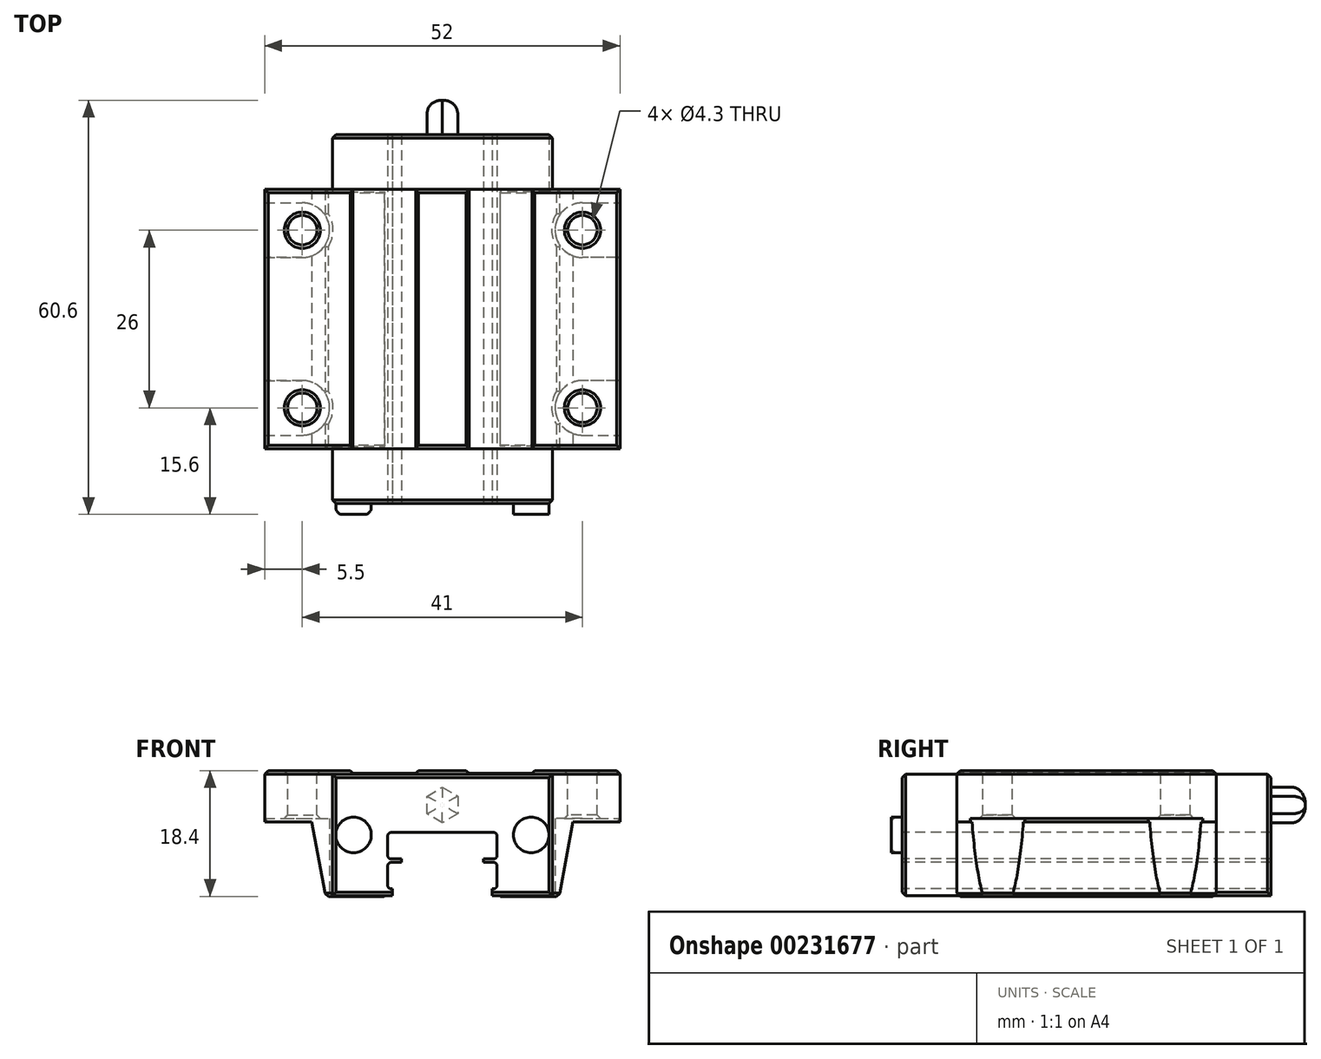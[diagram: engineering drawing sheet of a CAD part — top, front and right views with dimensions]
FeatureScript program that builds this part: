
annotation { "Feature Type Name" : "Feature", "Feature Type Description" : "" }
export const myFeature = defineFeature(function(context is Context, id is Id, definition is map)
    precondition{}
    {
        {
            var Q0;
            Q0=qCreatedBy(makeId("Front.planeOp"),FACE);
            var sketch = newSketch(context, id + "F0", { "sketchPlane" : qUnion([Q0])});
            skLineSegment(sketch, "E0", {"start": v(0, 7.25) * mm, "end": v(0, -7.25) * mm, "construction": true});
            skLineSegment(sketch, "E1", {"start": v(0, -7.25) * mm, "end": v(-7.5, -7.25) * mm});
            skLineSegment(sketch, "E2", {"start": v(-7.5, -7.25) * mm, "end": v(-7.5, -4.13) * mm});
            skLineSegment(sketch, "E3", {"start": v(-7.5, -4.13) * mm, "end": v(-7.5, -4.13) * mm});
            skLineSegment(sketch, "E4", {"start": v(-6.8, -3.43) * mm, "end": v(-6.8, -0.7) * mm});
            skLineSegment(sketch, "E5", {"start": v(-7.5, 0) * mm, "end": v(-7.5, 0) * mm});
            skLineSegment(sketch, "E6", {"start": v(-7.5, 0) * mm, "end": v(-7.5, 1.88) * mm});
            skLineSegment(sketch, "E7", {"start": v(-7.5, 1.88) * mm, "end": v(-7.5, 1.88) * mm});
            skLineSegment(sketch, "E8", {"start": v(-6.8, 2.88) * mm, "end": v(-5.5, 2.88) * mm});
            skLineSegment(sketch, "E9", {"start": v(-5.5, 2.88) * mm, "end": v(-5.5, 4.38) * mm});
            skLineSegment(sketch, "E10", {"start": v(-5.5, 4.38) * mm, "end": v(-6.8, 4.38) * mm});
            skLineSegment(sketch, "E11", {"start": v(-6.8, 4.38) * mm, "end": v(-6.8, 4.68) * mm});
            skLineSegment(sketch, "E12", {"start": v(-7.5, 5.38) * mm, "end": v(-7.5, 5.38) * mm});
            skLineSegment(sketch, "E13", {"start": v(-7.5, 5.38) * mm, "end": v(-7.5, 7.25) * mm});
            skLineSegment(sketch, "E14", {"start": v(-7.5, 7.25) * mm, "end": v(0, 7.25) * mm});
            skLineSegment(sketch, "E15", {"start": v(-6.8, 2.58) * mm, "end": v(-6.8, 2.87) * mm});
            skPoint(sketch, "E16.visualSharp", {"position": v(-6.8, -4.13) * mm});
            skArc(sketch, "E16.filletArc", {"start": v(-7.5, -4.13) * mm, "mid": v(-7, -3.92) * mm, "end": v(-6.8, -3.43) * mm});
            skPoint(sketch, "E17.visualSharp", {"position": v(-6.8, 0) * mm});
            skArc(sketch, "E17.filletArc", {"start": v(-6.8, -0.7) * mm, "mid": v(-7, -0.2) * mm, "end": v(-7.5, 0) * mm});
            skPoint(sketch, "E18.visualSharp", {"position": v(-6.8, 1.88) * mm});
            skArc(sketch, "E18.filletArc", {"start": v(-7.5, 1.88) * mm, "mid": v(-7, 2.08) * mm, "end": v(-6.8, 2.58) * mm});
            skPoint(sketch, "E19.visualSharp", {"position": v(-6.8, 5.38) * mm});
            skArc(sketch, "E19.filletArc", {"start": v(-6.8, 4.68) * mm, "mid": v(-7, 5.17) * mm, "end": v(-7.5, 5.38) * mm});
            skLineSegment(sketch, "E20.MirrorCS", {"start": v(6.8, 2.58) * mm, "end": v(6.8, 2.87) * mm});
            skLineSegment(sketch, "E21.MirrorCS", {"start": v(6.8, 4.38) * mm, "end": v(6.8, 4.68) * mm});
            skArc(sketch, "E22.MirrorCS", {"start": v(6.8, 4.68) * mm, "mid": v(7, 5.17) * mm, "end": v(7.5, 5.38) * mm});
            skArc(sketch, "E23.MirrorCS", {"start": v(7.5, 1.88) * mm, "mid": v(7, 2.08) * mm, "end": v(6.8, 2.58) * mm});
            skArc(sketch, "E24.MirrorCS", {"start": v(7.5, -4.13) * mm, "mid": v(7, -3.92) * mm, "end": v(6.8, -3.43) * mm});
            skArc(sketch, "E25.MirrorCS", {"start": v(6.8, -0.7) * mm, "mid": v(7, -0.2) * mm, "end": v(7.5, 0) * mm});
            skLineSegment(sketch, "E26.MirrorCS", {"start": v(7.5, 0) * mm, "end": v(7.5, 0) * mm});
            skLineSegment(sketch, "E27.MirrorCS", {"start": v(7.5, -7.25) * mm, "end": v(7.5, -4.13) * mm});
            skPoint(sketch, "E28.MirrorP", {"position": v(6.8, 0) * mm});
            skPoint(sketch, "E29.MirrorP", {"position": v(6.8, 5.38) * mm});
            skPoint(sketch, "E30.MirrorP", {"position": v(6.8, 1.88) * mm});
            skLineSegment(sketch, "E31.MirrorCS", {"start": v(7.5, -4.13) * mm, "end": v(7.5, -4.13) * mm});
            skLineSegment(sketch, "E32.MirrorCS", {"start": v(7.5, 1.88) * mm, "end": v(7.5, 1.88) * mm});
            skLineSegment(sketch, "E33.MirrorCS", {"start": v(7.5, 5.38) * mm, "end": v(7.5, 5.38) * mm});
            skLineSegment(sketch, "E34.MirrorCS", {"start": v(7.5, 5.38) * mm, "end": v(7.5, 7.25) * mm});
            skLineSegment(sketch, "E35.MirrorCS", {"start": v(5.5, 4.38) * mm, "end": v(6.8, 4.38) * mm});
            skLineSegment(sketch, "E36.MirrorCS", {"start": v(6.8, -3.43) * mm, "end": v(6.8, -0.7) * mm});
            skPoint(sketch, "E37.MirrorP", {"position": v(6.8, -4.13) * mm});
            skLineSegment(sketch, "E38.MirrorCS", {"start": v(6.8, 2.88) * mm, "end": v(5.5, 2.88) * mm});
            skLineSegment(sketch, "E39.MirrorCS", {"start": v(7.5, 0) * mm, "end": v(7.5, 1.88) * mm});
            skLineSegment(sketch, "E40.MirrorCS", {"start": v(5.5, 2.88) * mm, "end": v(5.5, 4.38) * mm});
            skLineSegment(sketch, "E41.MirrorCS", {"start": v(7.5, 7.25) * mm, "end": v(0, 7.25) * mm});
            skLineSegment(sketch, "E42.MirrorCS", {"start": v(0, -7.25) * mm, "end": v(7.5, -7.25) * mm});
            skSolve(sketch);
        }
        {
            var Q0;
            Q0=qCreatedBy(makeId("Front.planeOp"),FACE);
            var sketch = newSketch(context, id + "F1", { "sketchPlane" : qUnion([Q0])});
            skLineSegment(sketch, "E43", {"start": v(-16.1, 16.3) * mm, "end": v(-16.1, -1.5) * mm});
            skLineSegment(sketch, "E44", {"start": v(-16.1, -1.5) * mm, "end": v(-7.3, -1.5) * mm});
            skLineSegment(sketch, "E45", {"start": v(-7.3, -1.5) * mm, "end": v(-7.3, -0.5) * mm});
            skLineSegment(sketch, "E46", {"start": v(-7.3, -0.5) * mm, "end": v(-7.5, -0.5) * mm});
            skLineSegment(sketch, "E47", {"start": v(-8, 0) * mm, "end": v(-8, 2.88) * mm});
            skLineSegment(sketch, "E48", {"start": v(-7.5, 3.38) * mm, "end": v(-6, 3.38) * mm});
            skLineSegment(sketch, "E49", {"start": v(-6, 3.38) * mm, "end": v(-6, 3.88) * mm});
            skLineSegment(sketch, "E50", {"start": v(-6, 3.88) * mm, "end": v(-7.5, 3.88) * mm});
            skLineSegment(sketch, "E51", {"start": v(-8, 4.38) * mm, "end": v(-8, 7.25) * mm});
            skLineSegment(sketch, "E52", {"start": v(-7.5, 7.75) * mm, "end": v(0, 7.75) * mm});
            skLineSegment(sketch, "E53", {"start": v(-16.1, 16.3) * mm, "end": v(0, 16.3) * mm});
            skLineSegment(sketch, "E54", {"start": v(0, 16.3) * mm, "end": v(0, 0) * mm, "construction": true});
            skPoint(sketch, "E55.visualSharp", {"position": v(-8, 7.75) * mm});
            skArc(sketch, "E55.filletArc", {"start": v(-7.5, 7.75) * mm, "mid": v(-7.85, 7.6) * mm, "end": v(-8, 7.25) * mm});
            skPoint(sketch, "E56.visualSharp", {"position": v(-8, 3.88) * mm});
            skArc(sketch, "E56.filletArc", {"start": v(-8, 4.38) * mm, "mid": v(-7.85, 4.02) * mm, "end": v(-7.5, 3.88) * mm});
            skPoint(sketch, "E57.visualSharp", {"position": v(-8, 3.38) * mm});
            skArc(sketch, "E57.filletArc", {"start": v(-7.5, 3.38) * mm, "mid": v(-7.85, 3.23) * mm, "end": v(-8, 2.88) * mm});
            skPoint(sketch, "E58.visualSharp", {"position": v(-8, -0.5) * mm});
            skArc(sketch, "E58.filletArc", {"start": v(-8, 0) * mm, "mid": v(-7.85, -0.35) * mm, "end": v(-7.5, -0.5) * mm});
            skArc(sketch, "E59.MirrorCS", {"start": v(7.5, 7.75) * mm, "mid": v(7.85, 7.6) * mm, "end": v(8, 7.25) * mm});
            skArc(sketch, "E60.MirrorCS", {"start": v(7.5, 3.38) * mm, "mid": v(7.85, 3.23) * mm, "end": v(8, 2.88) * mm});
            skArc(sketch, "E61.MirrorCS", {"start": v(8, 0) * mm, "mid": v(7.85, -0.35) * mm, "end": v(7.5, -0.5) * mm});
            skLineSegment(sketch, "E62.MirrorCS", {"start": v(7.3, -0.5) * mm, "end": v(7.5, -0.5) * mm});
            skArc(sketch, "E63.MirrorCS", {"start": v(8, 4.38) * mm, "mid": v(7.85, 4.02) * mm, "end": v(7.5, 3.88) * mm});
            skLineSegment(sketch, "E64.MirrorCS", {"start": v(6, 3.88) * mm, "end": v(7.5, 3.88) * mm});
            skLineSegment(sketch, "E65.MirrorCS", {"start": v(8, 4.38) * mm, "end": v(8, 7.25) * mm});
            skLineSegment(sketch, "E66.MirrorCS", {"start": v(7.5, 3.38) * mm, "end": v(6, 3.38) * mm});
            skLineSegment(sketch, "E67.MirrorCS", {"start": v(7.3, -1.5) * mm, "end": v(7.3, -0.5) * mm});
            skLineSegment(sketch, "E68.MirrorCS", {"start": v(8, 0) * mm, "end": v(8, 2.88) * mm});
            skLineSegment(sketch, "E69.MirrorCS", {"start": v(6, 3.38) * mm, "end": v(6, 3.88) * mm});
            skPoint(sketch, "E70.MirrorP", {"position": v(8, 3.38) * mm});
            skPoint(sketch, "E71.MirrorP", {"position": v(8, 3.88) * mm});
            skLineSegment(sketch, "E72.MirrorCS", {"start": v(7.5, 7.75) * mm, "end": v(0, 7.75) * mm});
            skPoint(sketch, "E73.MirrorP", {"position": v(8, -0.5) * mm});
            skLineSegment(sketch, "E74.MirrorCS", {"start": v(16.1, 16.3) * mm, "end": v(0, 16.3) * mm});
            skLineSegment(sketch, "E75.MirrorCS", {"start": v(16.1, 16.3) * mm, "end": v(16.1, -1.5) * mm});
            skLineSegment(sketch, "E76.MirrorCS", {"start": v(16.1, -1.5) * mm, "end": v(7.3, -1.5) * mm});
            skPoint(sketch, "E77.MirrorP", {"position": v(8, 7.75) * mm});
            skSolve(sketch);
        }
        {
            var Q0;
            Q0 = qSketchRegion(id + "F1", true);
            extrude(context, id + "F2", {"entities" : qUnion([Q0]), "oppositeDirection" : true, "depth" : 54 * mm});
        }
        {
            var Q0;
            Q0=qCreatedBy(makeId("Front.planeOp"),FACE);
            cPlane(context, id + "F3", {"entities" : qUnion([Q0]), "cplaneType" : CPlaneType.OFFSET, "offset" : 8 * mm, "oppositeDirection" : true, "width" : 150 * mm, "height" : 150 * mm});
        }
        {
            var Q0;
            Q0=qCreatedBy(id+"F3.planeOp",FACE);
            var sketch = newSketch(context, id + "F4", { "sketchPlane" : qUnion([Q0])});
            skLineSegment(sketch, "E78", {"start": v(-8, -1.6) * mm, "end": v(-17.1, -1.6) * mm});
            skLineSegment(sketch, "E79", {"start": v(-17.1, -1.6) * mm, "end": v(-19.1, 9.3) * mm});
            skLineSegment(sketch, "E80", {"start": v(-19.1, 9.3) * mm, "end": v(-26, 9.3) * mm});
            skLineSegment(sketch, "E81", {"start": v(-26, 9.3) * mm, "end": v(-26, 16.8) * mm});
            skLineSegment(sketch, "E82", {"start": v(0, 16.8) * mm, "end": v(0, 0) * mm, "construction": true});
            skLineSegment(sketch, "E83", {"start": v(-26, 16.8) * mm, "end": v(-13, 16.8) * mm});
            skLineSegment(sketch, "E84", {"start": v(-13, 16.8) * mm, "end": v(-13, 16.4) * mm});
            skLineSegment(sketch, "E85", {"start": v(-13, 16.4) * mm, "end": v(-4, 16.4) * mm});
            skLineSegment(sketch, "E86", {"start": v(-4, 16.4) * mm, "end": v(-4, 16.8) * mm});
            skLineSegment(sketch, "E87", {"start": v(-4, 16.8) * mm, "end": v(0, 16.8) * mm});
            skLineSegment(sketch, "E88", {"start": v(-8, -1.6) * mm, "end": v(-8, 7.75) * mm});
            skLineSegment(sketch, "E89", {"start": v(-8, 7.75) * mm, "end": v(0, 7.75) * mm});
            skLineSegment(sketch, "E90.MirrorCS", {"start": v(4, 16.4) * mm, "end": v(4, 16.8) * mm});
            skLineSegment(sketch, "E91.MirrorCS", {"start": v(13, 16.8) * mm, "end": v(13, 16.4) * mm});
            skLineSegment(sketch, "E92.MirrorCS", {"start": v(8, -1.6) * mm, "end": v(8, 7.75) * mm});
            skLineSegment(sketch, "E93.MirrorCS", {"start": v(4, 16.8) * mm, "end": v(0, 16.8) * mm});
            skLineSegment(sketch, "E94.MirrorCS", {"start": v(26, 16.8) * mm, "end": v(13, 16.8) * mm});
            skLineSegment(sketch, "E95.MirrorCS", {"start": v(26, 9.3) * mm, "end": v(26, 16.8) * mm});
            skLineSegment(sketch, "E96.MirrorCS", {"start": v(8, -1.6) * mm, "end": v(17.1, -1.6) * mm});
            skLineSegment(sketch, "E97.MirrorCS", {"start": v(17.1, -1.6) * mm, "end": v(19.1, 9.3) * mm});
            skLineSegment(sketch, "E98.MirrorCS", {"start": v(8, 7.75) * mm, "end": v(0, 7.75) * mm});
            skLineSegment(sketch, "E99.MirrorCS", {"start": v(19.1, 9.3) * mm, "end": v(26, 9.3) * mm});
            skLineSegment(sketch, "E100.MirrorCS", {"start": v(13, 16.4) * mm, "end": v(4, 16.4) * mm});
            skSolve(sketch);
        }
        {
            var Q0;
            Q0 = qSketchRegion(id + "F4", true);
            extrude(context, id + "F5", {"entities" : qUnion([Q0]), "operationType" : NewBodyOperationType.ADD, "oppositeDirection" : true, "depth" : 38 * mm});
        }
        {
            var Q0;
            Q0=makeQuery(id+"F5.opExtrude","SWEPT_FACE",FACE,{"disambiguationData":[OSD([sQuery(id+"F4.wireOp",EDGE,"E83")])]});
            var sketch = newSketch(context, id + "F6", { "sketchPlane" : qUnion([Q0])});
            skCircle(sketch, "E101", {"center": v(-20.5, 40) * mm, "radius": 2.15 * mm});
            skCircle(sketch, "E102", {"center": v(-20.5, 14) * mm, "radius": 2.15 * mm});
            skLineSegment(sketch, "E103", {"start": v(-26, 27) * mm, "end": v(-13, 27) * mm, "construction": true});
            skCircle(sketch, "E104.MirrorC", {"center": v(20.5, 40) * mm, "radius": 2.15 * mm});
            skCircle(sketch, "E105.MirrorC", {"center": v(20.5, 14) * mm, "radius": 2.15 * mm});
            skSolve(sketch);
        }
        {
            var Q0;
            Q0 = qSketchRegion(id + "F6", true);
            extrude(context, id + "F7", {"entities" : qUnion([Q0]), "operationType" : NewBodyOperationType.REMOVE, "endBound" : BoundingType.THROUGH_ALL, "oppositeDirection" : true, "depth" : 25 * mm});
        }
        {
            var Q0;
            Q0=makeQuery(id+"F5.opExtrude","SWEPT_FACE",FACE,{"disambiguationData":[OSD([sQuery(id+"F4.wireOp",EDGE,"E80")])]});
            var sketch = newSketch(context, id + "F8", { "sketchPlane" : qUnion([Q0])});
            skArc(sketch, "E106", {"start": v(-20.5, -18) * mm, "mid": v(-16.5, -14) * mm, "end": v(-20.5, -10) * mm});
            skLineSegment(sketch, "E107", {"start": v(-26, -27) * mm, "end": v(-19.1, -27) * mm, "construction": true});
            skLineSegment(sketch, "E108", {"start": v(-20.5, -10) * mm, "end": v(-26, -10) * mm});
            skLineSegment(sketch, "E109", {"start": v(-26, -10) * mm, "end": v(-26, -18) * mm});
            skLineSegment(sketch, "E110", {"start": v(-26, -18) * mm, "end": v(-20.5, -18) * mm});
            skLineSegment(sketch, "E111.MirrorCS", {"start": v(-26, -36) * mm, "end": v(-20.5, -36) * mm});
            skLineSegment(sketch, "E112.MirrorCS", {"start": v(-26, -44) * mm, "end": v(-26, -36) * mm});
            skLineSegment(sketch, "E113.MirrorCS", {"start": v(-20.5, -44) * mm, "end": v(-26, -44) * mm});
            skArc(sketch, "E114.MirrorCS", {"start": v(-20.5, -36) * mm, "mid": v(-16.5, -40) * mm, "end": v(-20.5, -44) * mm});
            skArc(sketch, "E115.MirrorCS", {"start": v(20.5, -18) * mm, "mid": v(16.5, -14) * mm, "end": v(20.5, -10) * mm});
            skLineSegment(sketch, "E116.MirrorCS", {"start": v(26, -18) * mm, "end": v(20.5, -18) * mm});
            skLineSegment(sketch, "E117.MirrorCS", {"start": v(26, -10) * mm, "end": v(26, -18) * mm});
            skLineSegment(sketch, "E118.MirrorCS", {"start": v(20.5, -10) * mm, "end": v(26, -10) * mm});
            skLineSegment(sketch, "E119.MirrorCS", {"start": v(26, -36) * mm, "end": v(20.5, -36) * mm});
            skArc(sketch, "E120.MirrorCS", {"start": v(20.5, -36) * mm, "mid": v(16.5, -40) * mm, "end": v(20.5, -44) * mm});
            skLineSegment(sketch, "E121.MirrorCS", {"start": v(20.5, -44) * mm, "end": v(26, -44) * mm});
            skLineSegment(sketch, "E122.MirrorCS", {"start": v(26, -44) * mm, "end": v(26, -36) * mm});
            skSolve(sketch);
        }
        {
            var Q0;
            Q0 = qSketchRegion(id + "F8", true);
            extrude(context, id + "F9", {"entities" : qUnion([Q0]), "operationType" : NewBodyOperationType.REMOVE, "oppositeDirection" : true, "depth" : 0.5 * mm, "hasSecondDirection" : true, "secondDirectionBound" : SecondDirectionBoundingType.THROUGH_ALL, "secondDirectionOppositeDirection" : false, "secondDirectionDepth" : 25 * mm});
        }
        {
            var Q0;
            Q0=makeQuery(id+"F5.opExtrude","SWEPT_FACE",FACE,{"disambiguationData":[OSD([sQuery(id+"F4.wireOp",EDGE,"E78")])]});
            var Q1;
            Q1=makeQuery(id+"F5.opExtrude","SWEPT_FACE",FACE,{"disambiguationData":[OSD([sQuery(id+"F4.wireOp",EDGE,"E96.MirrorCS")])]});
            var Q2;
            Q2=makeQuery(id+"F7.boolean.opBoolean","COPY",FACE,{"derivedFrom":makeQuery(id+"F7.opExtrude","SWEPT_FACE",FACE,{"disambiguationData":[OSD([sQuery(id+"F6.wireOp",EDGE,"E101")])]})});
            var Q3;
            Q3=makeQuery(id+"F7.boolean.opBoolean","COPY",FACE,{"derivedFrom":makeQuery(id+"F7.opExtrude","SWEPT_FACE",FACE,{"disambiguationData":[OSD([sQuery(id+"F6.wireOp",EDGE,"E102")])]})});
            var Q4;
            Q4=makeQuery(id+"F7.boolean.opBoolean","COPY",FACE,{"derivedFrom":makeQuery(id+"F7.opExtrude","SWEPT_FACE",FACE,{"disambiguationData":[OSD([sQuery(id+"F6.wireOp",EDGE,"E105.MirrorC")])]})});
            var Q5;
            Q5=makeQuery(id+"F7.boolean.opBoolean","COPY",FACE,{"derivedFrom":makeQuery(id+"F7.opExtrude","SWEPT_FACE",FACE,{"disambiguationData":[OSD([sQuery(id+"F6.wireOp",EDGE,"E104.MirrorC")])]})});
            var Q6;
            Q6=makeQuery(id+"F5.opExtrude","SWEPT_FACE",FACE,{"disambiguationData":[OSD([sQuery(id+"F4.wireOp",EDGE,"E87"),sQuery(id+"F4.wireOp",EDGE,"E93.MirrorCS")])]});
            var Q7;
            Q7=makeQuery(id+"F5.opExtrude","SWEPT_FACE",FACE,{"disambiguationData":[OSD([sQuery(id+"F4.wireOp",EDGE,"E94.MirrorCS")])]});
            var Q8;
            Q8=makeQuery(id+"F5.opExtrude","SWEPT_FACE",FACE,{"disambiguationData":[OSD([sQuery(id+"F4.wireOp",EDGE,"E83")])]});
            chamfer(context, id + "F10", {"entities" : qUnion([Q0, Q1, Q2, Q3, Q4, Q5, Q6, Q7, Q8]), "width" : 0.5 * mm, "tangentPropagation" : true});
        }
        {
            var Q0;
            {var subQ0=sQuery(id+"F4.wireOp",EDGE,"E95.MirrorCS");var subQ1=sQuery(id+"F4.wireOp",EDGE,"E99.MirrorCS");Q0=makeQuery(id+"F9.boolean.opBoolean","SPLIT",EDGE,{"disambiguationData":[TD([makeQuery(id+"F9.opExtrude","SWEPT_FACE",FACE,{"disambiguationData":[OSD([sQuery(id+"F8.wireOp",EDGE,"E116.MirrorCS")])]})])],"derivedFrom":makeQuery(id+"F5.opExtrude","SWEPT_EDGE",EDGE,{"disambiguationData":[OSD([subQ0,subQ1])]})});}
            var Q1;
            {var subQ0=sQuery(id+"F1.wireOp",EDGE,"E76.MirrorCS");var subQ1=sQuery(id+"F1.wireOp",EDGE,"E75.MirrorCS");Q1=makeQuery(id+"F5.boolean.opBoolean","SPLIT",EDGE,{"disambiguationData":[TD([makeQuery(id+"F5.opExtrude","CAP_FACE",FACE,{"disambiguationData":[OSD([sQuery(id+"F4.wireOp",EDGE,"E78"),sQuery(id+"F4.wireOp",EDGE,"E79"),sQuery(id+"F4.wireOp",EDGE,"E80"),sQuery(id+"F4.wireOp",EDGE,"E81"),sQuery(id+"F4.wireOp",EDGE,"E83"),sQuery(id+"F4.wireOp",EDGE,"E84"),sQuery(id+"F4.wireOp",EDGE,"E85"),sQuery(id+"F4.wireOp",EDGE,"E86"),sQuery(id+"F4.wireOp",EDGE,"E87"),sQuery(id+"F4.wireOp",EDGE,"E88"),sQuery(id+"F4.wireOp",EDGE,"E89"),sQuery(id+"F4.wireOp",EDGE,"E90.MirrorCS"),sQuery(id+"F4.wireOp",EDGE,"E91.MirrorCS"),sQuery(id+"F4.wireOp",EDGE,"E92.MirrorCS"),sQuery(id+"F4.wireOp",EDGE,"E93.MirrorCS"),sQuery(id+"F4.wireOp",EDGE,"E94.MirrorCS"),sQuery(id+"F4.wireOp",EDGE,"E95.MirrorCS"),sQuery(id+"F4.wireOp",EDGE,"E96.MirrorCS"),sQuery(id+"F4.wireOp",EDGE,"E97.MirrorCS"),sQuery(id+"F4.wireOp",EDGE,"E98.MirrorCS"),sQuery(id+"F4.wireOp",EDGE,"E99.MirrorCS"),sQuery(id+"F4.wireOp",EDGE,"E100.MirrorCS")])],"isStart":false})])],"derivedFrom":makeQuery(id+"F2.opExtrude","SWEPT_EDGE",EDGE,{"disambiguationData":[OSD([subQ1,subQ0])]})});}
            var Q2;
            Q2=makeQuery(id+"F2.opExtrude","CAP_EDGE",EDGE,{"disambiguationData":[OSD([sQuery(id+"F1.wireOp",EDGE,"E75.MirrorCS")])],"isStart":false});
            var Q3;
            Q3=makeQuery(id+"F2.opExtrude","CAP_EDGE",EDGE,{"disambiguationData":[OSD([sQuery(id+"F1.wireOp",EDGE,"E53"),sQuery(id+"F1.wireOp",EDGE,"E74.MirrorCS")])],"isStart":false});
            var Q4;
            Q4=makeQuery(id+"F2.opExtrude","CAP_EDGE",EDGE,{"disambiguationData":[OSD([sQuery(id+"F1.wireOp",EDGE,"E43")])],"isStart":false});
            var Q5;
            Q5=makeQuery(id+"F2.opExtrude","CAP_EDGE",EDGE,{"disambiguationData":[OSD([sQuery(id+"F1.wireOp",EDGE,"E44")])],"isStart":false});
            var Q6;
            Q6=makeQuery(id+"F2.opExtrude","CAP_EDGE",EDGE,{"disambiguationData":[OSD([sQuery(id+"F1.wireOp",EDGE,"E43")])],"isStart":true});
            var Q7;
            Q7=makeQuery(id+"F2.opExtrude","CAP_EDGE",EDGE,{"disambiguationData":[OSD([sQuery(id+"F1.wireOp",EDGE,"E44")])],"isStart":true});
            var Q8;
            Q8=makeQuery(id+"F2.opExtrude","CAP_EDGE",EDGE,{"disambiguationData":[OSD([sQuery(id+"F1.wireOp",EDGE,"E76.MirrorCS")])],"isStart":true});
            var Q9;
            Q9=makeQuery(id+"F2.opExtrude","CAP_EDGE",EDGE,{"disambiguationData":[OSD([sQuery(id+"F1.wireOp",EDGE,"E75.MirrorCS")])],"isStart":true});
            var Q10;
            Q10=makeQuery(id+"F2.opExtrude","CAP_EDGE",EDGE,{"disambiguationData":[OSD([sQuery(id+"F1.wireOp",EDGE,"E53"),sQuery(id+"F1.wireOp",EDGE,"E74.MirrorCS")])],"isStart":true});
            var Q11;
            {var subQ0=sQuery(id+"F4.wireOp",EDGE,"E80");var subQ1=sQuery(id+"F4.wireOp",EDGE,"E81");Q11=makeQuery(id+"F9.boolean.opBoolean","SPLIT",EDGE,{"disambiguationData":[TD([makeQuery(id+"F9.opExtrude","SWEPT_FACE",FACE,{"disambiguationData":[OSD([sQuery(id+"F8.wireOp",EDGE,"E110")])]})])],"derivedFrom":makeQuery(id+"F5.opExtrude","SWEPT_EDGE",EDGE,{"disambiguationData":[OSD([subQ0,subQ1])]})});}
            chamfer(context, id + "F11", {"entities" : qUnion([Q0, Q1, Q2, Q3, Q4, Q5, Q6, Q7, Q8, Q9, Q10, Q11]), "width" : 0.5 * mm, "tangentPropagation" : true});
        }
        {
            var Q0;
            Q0=makeQuery(id+"F2.opExtrude","CAP_FACE",FACE,{"disambiguationData":[OSD([sQuery(id+"F1.wireOp",EDGE,"E43"),sQuery(id+"F1.wireOp",EDGE,"E44"),sQuery(id+"F1.wireOp",EDGE,"E45"),sQuery(id+"F1.wireOp",EDGE,"E46"),sQuery(id+"F1.wireOp",EDGE,"E47"),sQuery(id+"F1.wireOp",EDGE,"E48"),sQuery(id+"F1.wireOp",EDGE,"E49"),sQuery(id+"F1.wireOp",EDGE,"E50"),sQuery(id+"F1.wireOp",EDGE,"E51"),sQuery(id+"F1.wireOp",EDGE,"E52"),sQuery(id+"F1.wireOp",EDGE,"E53"),sQuery(id+"F1.wireOp",EDGE,"E55.filletArc"),sQuery(id+"F1.wireOp",EDGE,"E56.filletArc"),sQuery(id+"F1.wireOp",EDGE,"E57.filletArc"),sQuery(id+"F1.wireOp",EDGE,"E58.filletArc"),sQuery(id+"F1.wireOp",EDGE,"E59.MirrorCS"),sQuery(id+"F1.wireOp",EDGE,"E60.MirrorCS"),sQuery(id+"F1.wireOp",EDGE,"E61.MirrorCS"),sQuery(id+"F1.wireOp",EDGE,"E62.MirrorCS"),sQuery(id+"F1.wireOp",EDGE,"E63.MirrorCS"),sQuery(id+"F1.wireOp",EDGE,"E64.MirrorCS"),sQuery(id+"F1.wireOp",EDGE,"E65.MirrorCS"),sQuery(id+"F1.wireOp",EDGE,"E66.MirrorCS"),sQuery(id+"F1.wireOp",EDGE,"E67.MirrorCS"),sQuery(id+"F1.wireOp",EDGE,"E68.MirrorCS"),sQuery(id+"F1.wireOp",EDGE,"E69.MirrorCS"),sQuery(id+"F1.wireOp",EDGE,"E72.MirrorCS"),sQuery(id+"F1.wireOp",EDGE,"E74.MirrorCS"),sQuery(id+"F1.wireOp",EDGE,"E75.MirrorCS"),sQuery(id+"F1.wireOp",EDGE,"E76.MirrorCS")])],"isStart":true});
            var sketch = newSketch(context, id + "F12", { "sketchPlane" : qUnion([Q0])});
            skLineSegment(sketch, "E123", {"start": v(-15.6, 7.4) * mm, "end": v(15.6, 7.4) * mm, "construction": true});
            skCircle(sketch, "E124", {"center": v(-13, 7.4) * mm, "radius": 2.6 * mm});
            skLineSegment(sketch, "E125", {"start": v(0, 0) * mm, "end": v(0, 15.8) * mm, "construction": true});
            skCircle(sketch, "E126", {"center": v(13, 7.4) * mm, "radius": 2.6 * mm});
            skSolve(sketch);
        }
        {
            var Q0;
            Q0 = qSketchRegion(id + "F12", true);
            extrude(context, id + "F13", {"entities" : qUnion([Q0]), "operationType" : NewBodyOperationType.ADD, "depth" : 1.6 * mm});
        }
        {
            var Q0;
            Q0=makeQuery(id+"F2.opExtrude","CAP_FACE",FACE,{"disambiguationData":[OSD([sQuery(id+"F1.wireOp",EDGE,"E43"),sQuery(id+"F1.wireOp",EDGE,"E44"),sQuery(id+"F1.wireOp",EDGE,"E45"),sQuery(id+"F1.wireOp",EDGE,"E46"),sQuery(id+"F1.wireOp",EDGE,"E47"),sQuery(id+"F1.wireOp",EDGE,"E48"),sQuery(id+"F1.wireOp",EDGE,"E49"),sQuery(id+"F1.wireOp",EDGE,"E50"),sQuery(id+"F1.wireOp",EDGE,"E51"),sQuery(id+"F1.wireOp",EDGE,"E52"),sQuery(id+"F1.wireOp",EDGE,"E53"),sQuery(id+"F1.wireOp",EDGE,"E55.filletArc"),sQuery(id+"F1.wireOp",EDGE,"E56.filletArc"),sQuery(id+"F1.wireOp",EDGE,"E57.filletArc"),sQuery(id+"F1.wireOp",EDGE,"E58.filletArc"),sQuery(id+"F1.wireOp",EDGE,"E59.MirrorCS"),sQuery(id+"F1.wireOp",EDGE,"E60.MirrorCS"),sQuery(id+"F1.wireOp",EDGE,"E61.MirrorCS"),sQuery(id+"F1.wireOp",EDGE,"E62.MirrorCS"),sQuery(id+"F1.wireOp",EDGE,"E63.MirrorCS"),sQuery(id+"F1.wireOp",EDGE,"E64.MirrorCS"),sQuery(id+"F1.wireOp",EDGE,"E65.MirrorCS"),sQuery(id+"F1.wireOp",EDGE,"E66.MirrorCS"),sQuery(id+"F1.wireOp",EDGE,"E67.MirrorCS"),sQuery(id+"F1.wireOp",EDGE,"E68.MirrorCS"),sQuery(id+"F1.wireOp",EDGE,"E69.MirrorCS"),sQuery(id+"F1.wireOp",EDGE,"E72.MirrorCS"),sQuery(id+"F1.wireOp",EDGE,"E74.MirrorCS"),sQuery(id+"F1.wireOp",EDGE,"E75.MirrorCS"),sQuery(id+"F1.wireOp",EDGE,"E76.MirrorCS")])],"isStart":false});
            var sketch = newSketch(context, id + "F14", { "sketchPlane" : qUnion([Q0])});
            skLineSegment(sketch, "E127", {"start": v(0, 15.8) * mm, "end": v(0, 7.75) * mm, "construction": true});
            skCircle(sketch, "E128", {"center": v(0, 11.78) * mm, "radius": 2.6 * mm, "construction": true});
            skLineSegment(sketch, "E129", {"start": v(-2.25, 13.07) * mm, "end": v(-2.25, 10.48) * mm});
            skLineSegment(sketch, "E130", {"start": v(-2.25, 10.48) * mm, "end": v(0, 9.18) * mm});
            skLineSegment(sketch, "E131", {"start": v(0, 9.18) * mm, "end": v(2.25, 10.48) * mm});
            skLineSegment(sketch, "E132", {"start": v(2.25, 10.48) * mm, "end": v(2.25, 13.07) * mm});
            skLineSegment(sketch, "E133", {"start": v(2.25, 13.07) * mm, "end": v(0, 14.37) * mm});
            skLineSegment(sketch, "E134", {"start": v(0, 14.37) * mm, "end": v(-2.25, 13.07) * mm});
            skSolve(sketch);
        }
        {
            var Q0;
            Q0 = qSketchRegion(id + "F14", true);
            extrude(context, id + "F15", {"entities" : qUnion([Q0]), "operationType" : NewBodyOperationType.ADD, "depth" : 5 * mm});
        }
        {
            var Q0;
            Q0=makeQuery(id+"F15.opExtrude","CAP_FACE",FACE,{"disambiguationData":[OSD([sQuery(id+"F14.wireOp",EDGE,"E129"),sQuery(id+"F14.wireOp",EDGE,"E130"),sQuery(id+"F14.wireOp",EDGE,"E131"),sQuery(id+"F14.wireOp",EDGE,"E132"),sQuery(id+"F14.wireOp",EDGE,"E133"),sQuery(id+"F14.wireOp",EDGE,"E134")])],"isStart":false});
            fillet(context, id + "F16", {"entities" : qUnion([Q0]), "radius" : 2 * mm, "tangentPropagation" : true, "allowEdgeOverflow" : false});
        }
        {
            var Q0;
            Q0=makeQuery(id+"F13.opExtrude","CAP_EDGE",EDGE,{"disambiguationData":[OSD([sQuery(id+"F12.wireOp",EDGE,"E124")])],"isStart":false});
            fillet(context, id + "F17", {"entities" : qUnion([Q0]), "radius" : 1 * mm, "tangentPropagation" : true, "allowEdgeOverflow" : false});
        }
    });
